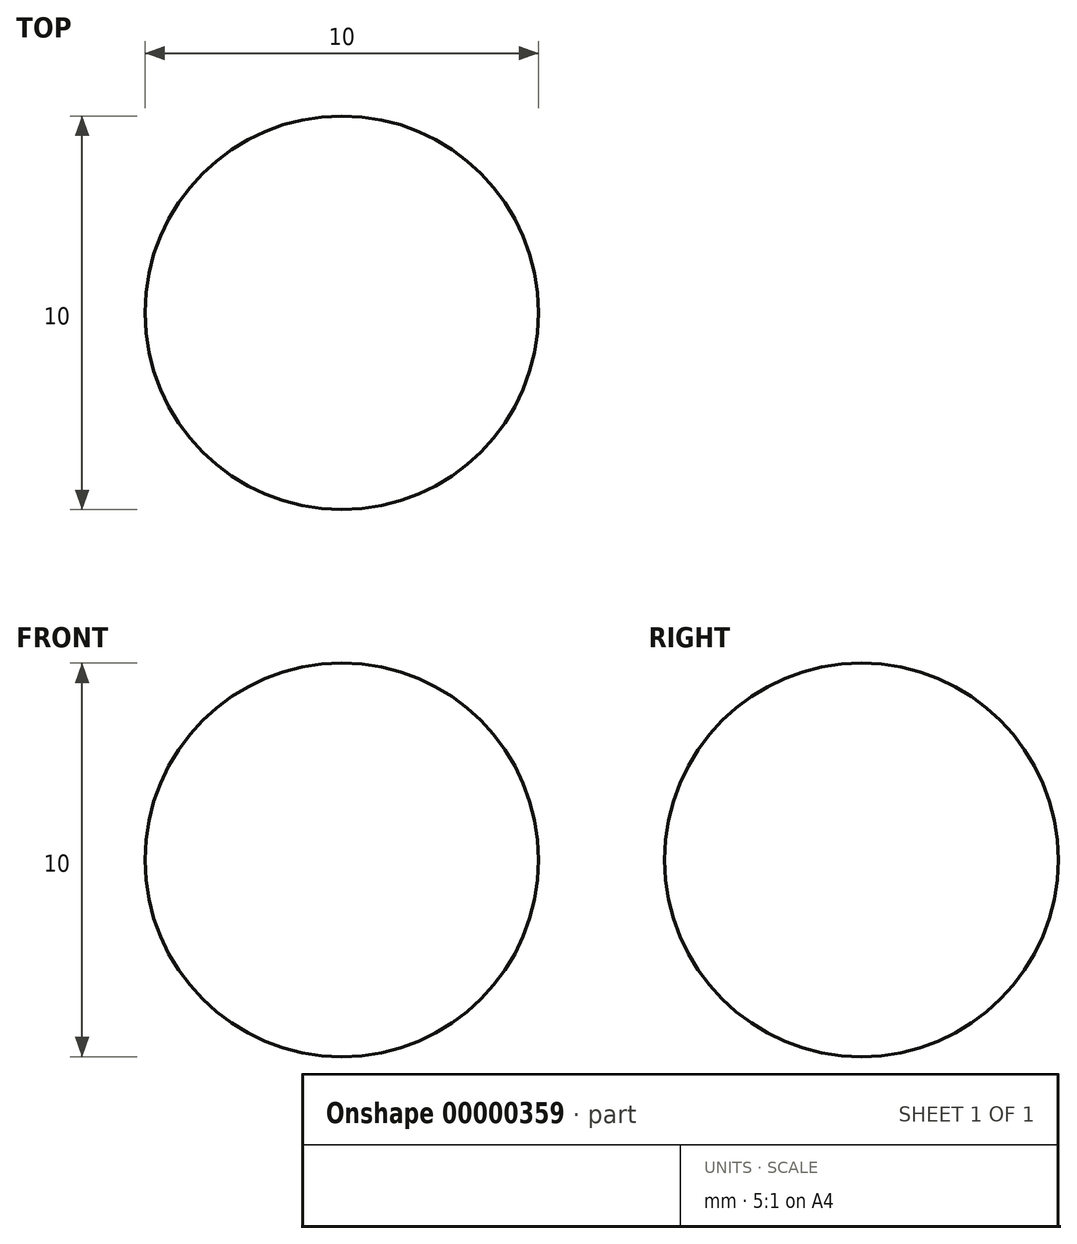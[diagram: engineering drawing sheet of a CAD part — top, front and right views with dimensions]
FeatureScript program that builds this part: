
annotation { "Feature Type Name" : "Feature", "Feature Type Description" : "" }
export const myFeature = defineFeature(function(context is Context, id is Id, definition is map)
    precondition{}
    {
        {
            var Q0;
            Q0 = qCreatedBy(makeId("Top.planeOp"), FACE);
            var sketch = newSketch(context, id + "F0", { "sketchPlane" : qUnion([Q0])});
            skArc(sketch, "E0", {"start": v(0, -5) * mm, "mid": v(5, 0) * mm, "end": v(0, 5) * mm});
            skLineSegment(sketch, "E1", {"start": v(0, -261.4) * mm, "end": v(0, 286.77) * mm, "construction": true});
            skLineSegment(sketch, "E2", {"start": v(0, 5) * mm, "end": v(0, -5) * mm});
            skSolve(sketch);
        }
        {
            var Q0;
            Q0=makeQuery(id+"F0.imprint","IMPRINT",FACE,{"disambiguationData":[TD([[makeQuery(id+"F0.imprint","IMPRINT",EDGE,{"derivedFrom":sQuery(id+"F0.wireOp",EDGE,"E0")}),1.0]])]});
            var Q1;
            Q1=sQuery(id+"F0.wireOp",EDGE,"E1");
            revolve(context, id + "F1", {"entities" : qUnion([Q0]), "axis" : qUnion([Q1]), "revolveType" : RevolveType.FULL});
        }
    });
